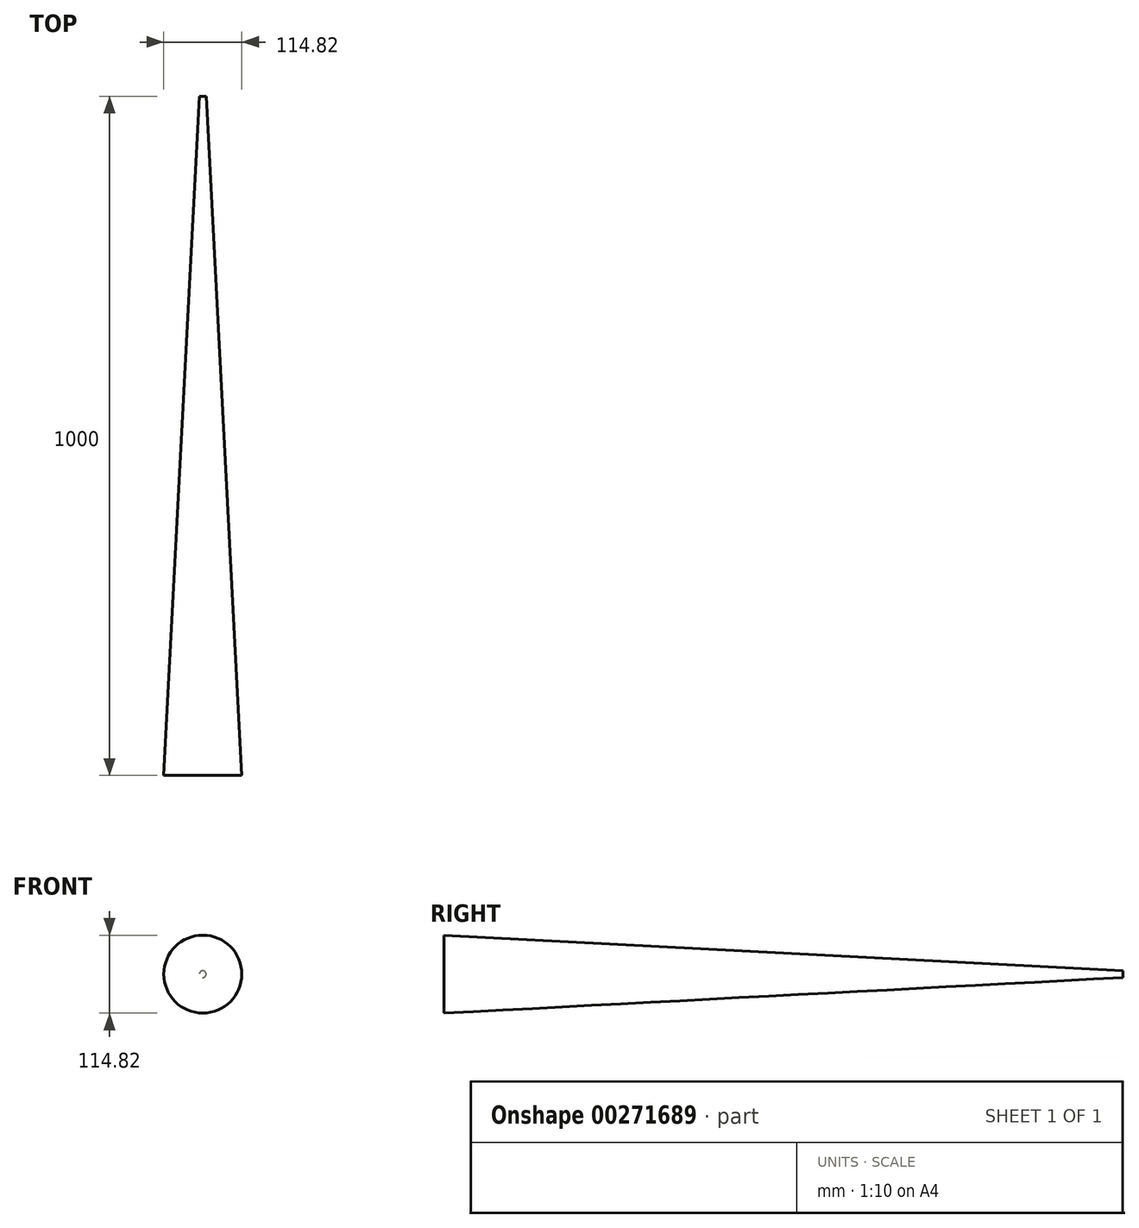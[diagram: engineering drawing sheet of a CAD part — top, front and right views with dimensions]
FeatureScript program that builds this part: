
annotation { "Feature Type Name" : "Feature", "Feature Type Description" : "" }
export const myFeature = defineFeature(function(context is Context, id is Id, definition is map)
    precondition{}
    {
        {
            var Q0;
            Q0=qCreatedBy(makeId("Front.planeOp"),FACE);
            var sketch = newSketch(context, id + "F0", { "sketchPlane" : qUnion([Q0])});
            skCircle(sketch, "E0", {"center": v(0, 0) * mm, "radius": 5 * mm});
            skSolve(sketch);
        }
        {
            var Q0;
            Q0 = qSketchRegion(id + "F0", true);
            extrude(context, id + "F1", {"entities" : qUnion([Q0]), "depth" : 1000 * mm, "hasDraft" : true, "draftAngle" : 3 * degree});
        }
    });
